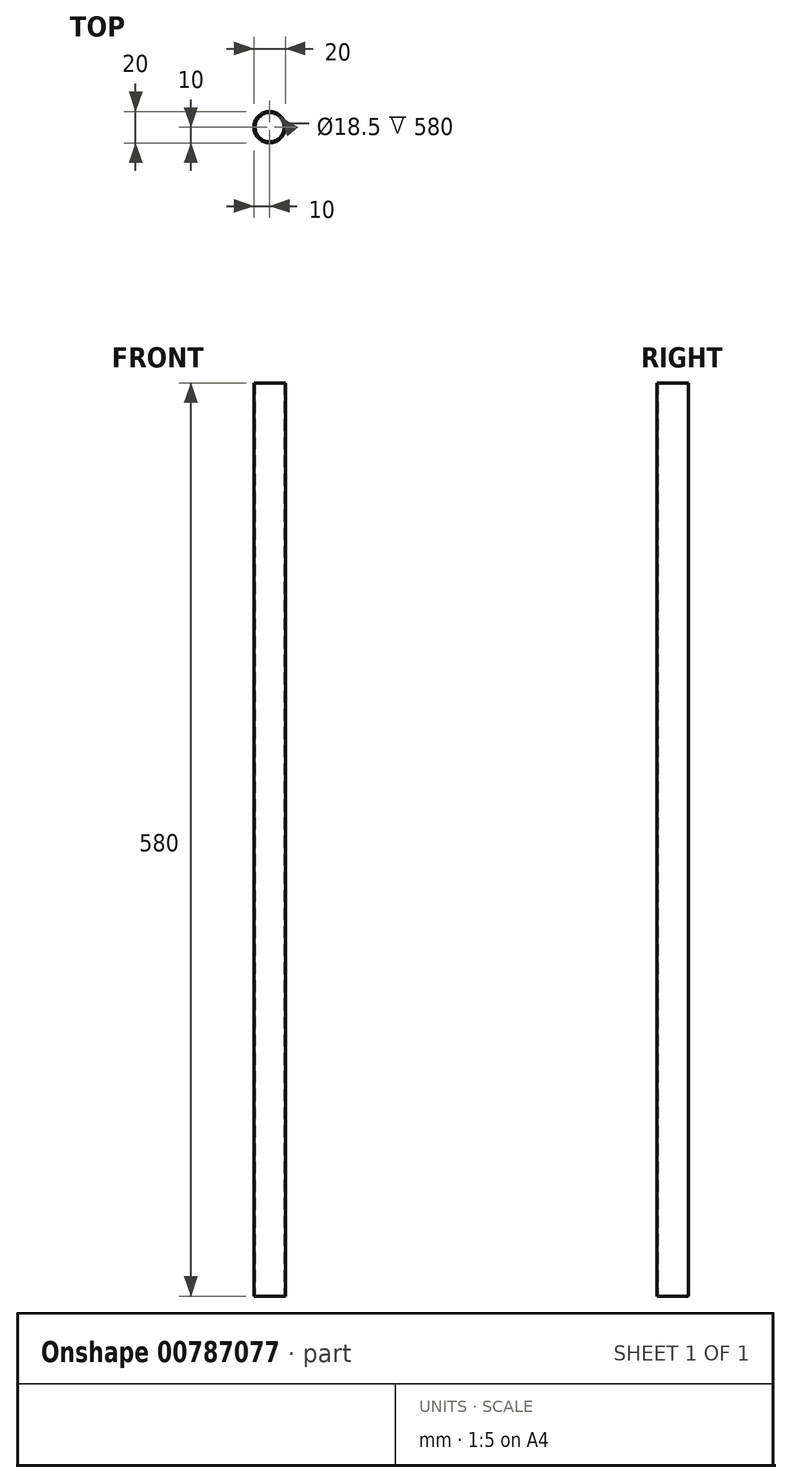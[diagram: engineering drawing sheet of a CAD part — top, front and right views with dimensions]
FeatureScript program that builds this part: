
annotation { "Feature Type Name" : "Feature", "Feature Type Description" : "" }
export const myFeature = defineFeature(function(context is Context, id is Id, definition is map)
    precondition{}
    {
        {
            var Q0;
            Q0=qCreatedBy(makeId("Top.planeOp"),FACE);
            var sketch = newSketch(context, id + "F0", { "sketchPlane" : qUnion([Q0])});
            skCircle(sketch, "E0", {"center": v(0, 0) * mm, "radius": 10 * mm});
            skCircle(sketch, "E1", {"center": v(0, 0) * mm, "radius": 9.25 * mm});
            skSolve(sketch);
        }
        {
            var Q0;
            Q0=makeQuery(id+"F0.imprint","IMPRINT",FACE,{"disambiguationData":[TD([[makeQuery(id+"F0.imprint","IMPRINT",EDGE,{"derivedFrom":sQuery(id+"F0.wireOp",EDGE,"E0")}),1.0]])]});
            extrude(context, id + "F1", {"entities" : qUnion([Q0]), "depth" : 580 * mm, "offsetDistance" : 25 * mm});
        }
    });
